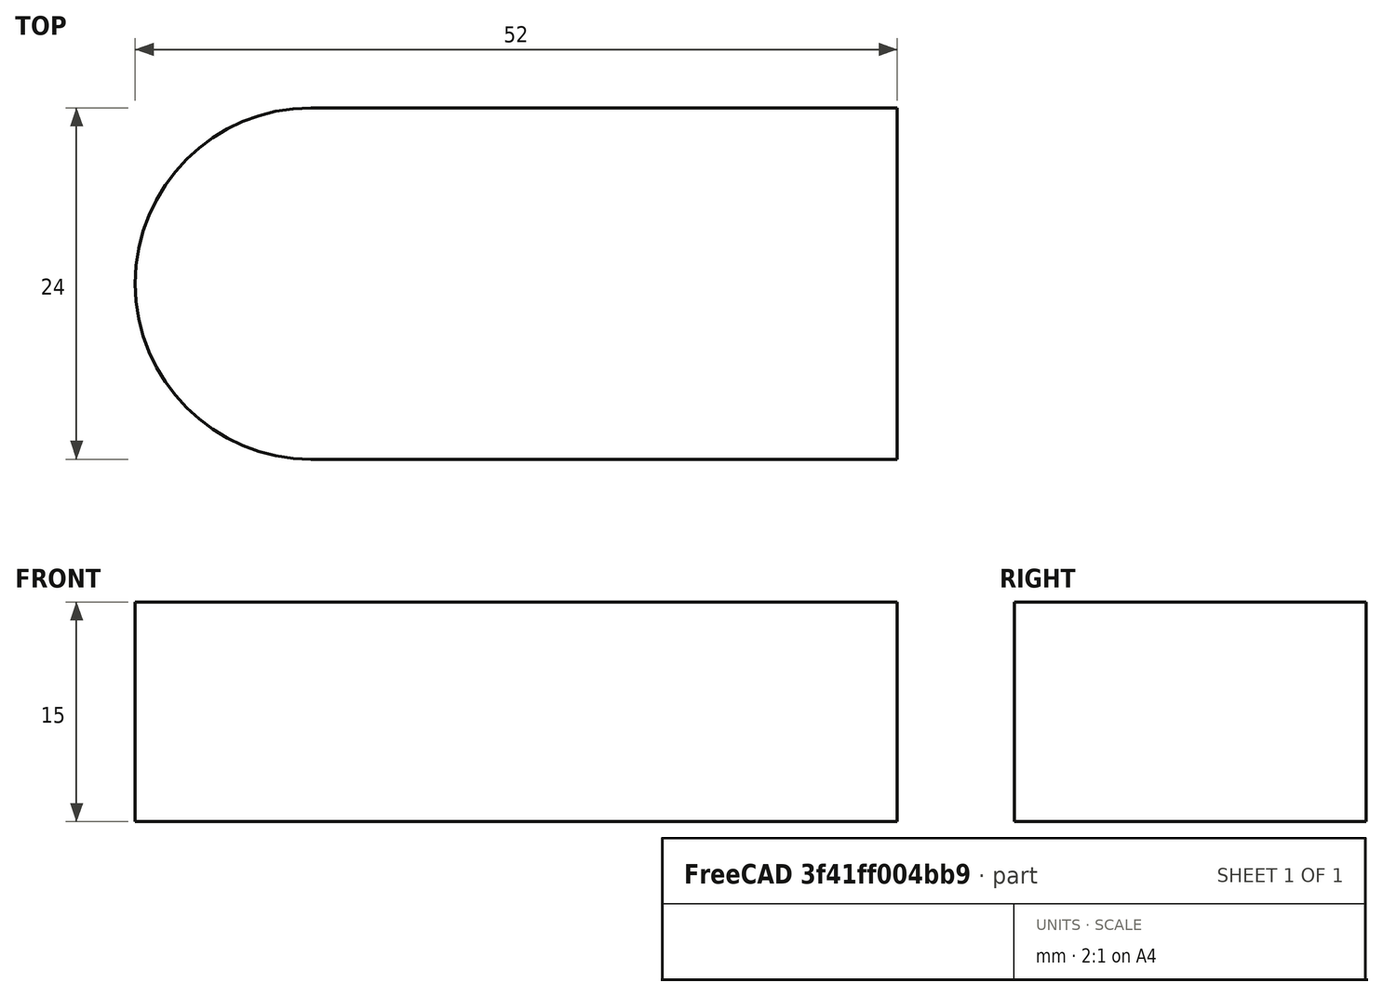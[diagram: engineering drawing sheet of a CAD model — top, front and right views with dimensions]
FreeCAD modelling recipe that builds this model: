
FCSTD DOCUMENT  (FreeCAD 0.20R29603 (Git))
Label: CorpoTrava
License: All rights reserved
LicenseURL: http://en.wikipedia.org/wiki/All_rights_reserved
objects: Sketcher::SketchObject×1, PartDesign::Pad×1, PartDesign::Body×1
note: 4 computed .brp shape members not serialized (recipe doc carries the construction recipe); baked Part::Feature solids carry a one-line shape summary decoded from their .brp

FEATURE [Sketcher::SketchObject] Sketch
  FullyConstrained = true
  MapMode = 5
  Support = -> [XY_Plane]
  sketch-geometry (5):
    g0: ArcOfCircle CenterX=0 CenterY=0 CenterZ=0 NormalX=0 NormalY=0 NormalZ=1 AngleXU=0 Radius=12 StartAngle=1.5708 EndAngle=4.71239
    g1: LineSegment StartX=7e-16 StartY=12 StartZ=0 EndX=40 EndY=12 EndZ=0
    g2: LineSegment StartX=40 StartY=12 StartZ=0 EndX=40 EndY=-12 EndZ=0
    g3: LineSegment StartX=40 StartY=-12 StartZ=0 EndX=0 EndY=-12 EndZ=0
    g4: GeomPoint X=15 Y=0 Z=0
  constraints (14):
    c: Coincident(g0,g-1)
    c: PointOnObject(g0,g-2)
    c: PointOnObject(g0,g-2)
    c: Radius(g0) = 12
    c: Coincident(g1,g0)
    c: Horizontal(g1)
    c: Coincident(g2,g1)
    c: Vertical(g2)
    c: Coincident(g3,g2)
    c: Coincident(g3,g0)
    c: Horizontal(g3)
    c: DistanceX(g3,g3) = 40
    c: PointOnObject(g4,g-1)
    c: Distance(g4,g2) = 25
FEATURE [PartDesign::Pad] Pad
  Direction = (0,0,1)
  Length = 15
  Length2 = 10
  Profile = -> Sketch
  ReferenceAxis = -> Sketch [N_Axis]
  Refine = true
  Type = 0
FEATURE [PartDesign::Body] Body
  Group = -> [Sketch,Pad]
  Origin = -> Origin
  Tip = -> Pad
